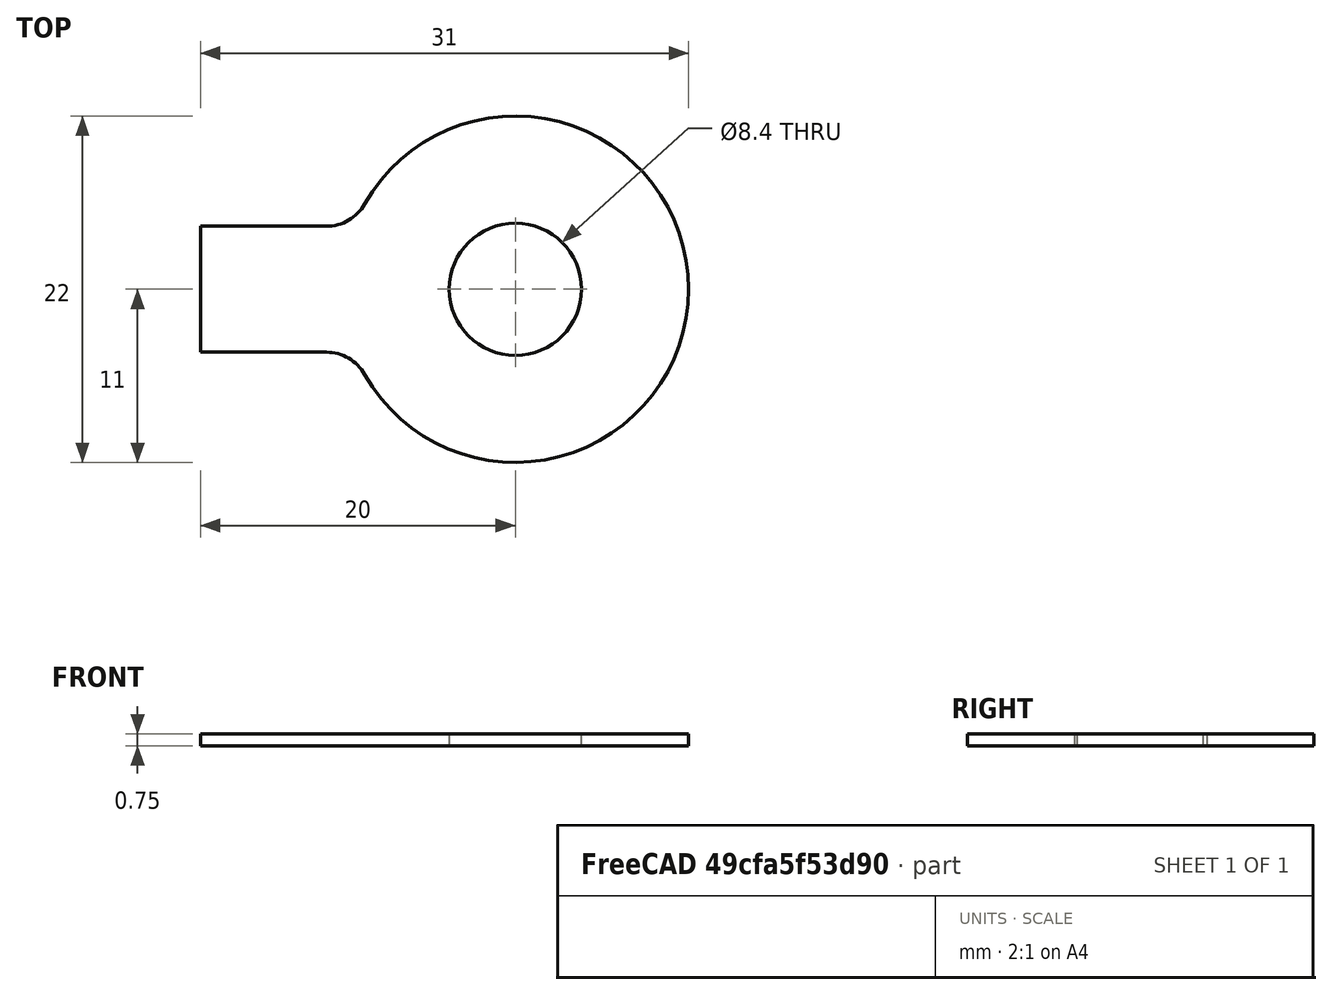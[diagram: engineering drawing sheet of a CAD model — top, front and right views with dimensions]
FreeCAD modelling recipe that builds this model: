
FCSTD DOCUMENT  (FreeCAD 0.15R4671 (Git))
Label: DIN93_M8TabWasher
License: CreativeCommons Attribution-ShareAlike
LicenseURL: http://creativecommons.org/licenses/by-sa/4.0/
objects: Sketcher::SketchObject×1, PartDesign::Pad×1
note: 3 computed .brp shape members not serialized (recipe doc carries the construction recipe); baked Part::Feature solids carry a one-line shape summary decoded from their .brp

FEATURE [Sketcher::SketchObject] Sketch
  sketch-geometry (7):
    g0: Circle CenterX=0 CenterY=0 CenterZ=0 NormalX=0 NormalY=0 NormalZ=1 Radius=4.2
    g1: LineSegment StartX=-20 StartY=4 StartZ=0 EndX=-12 EndY=4 EndZ=0
    g2: LineSegment StartX=-12 StartY=-4 StartZ=0 EndX=-20 EndY=-4 EndZ=0
    g3: LineSegment StartX=-20 StartY=-4 StartZ=0 EndX=-20 EndY=4 EndZ=0
    g4: ArcOfCircle CenterX=0 CenterY=0 CenterZ=0 NormalX=0 NormalY=0 NormalZ=1 Radius=11 StartAngle=3.65624 EndAngle=8.91013
    g5: ArcOfCircle CenterX=-12 CenterY=6.7857 CenterZ=0 NormalX=0 NormalY=0 NormalZ=1 Radius=2.7857 StartAngle=4.71239 EndAngle=5.76853
    g6: ArcOfCircle CenterX=-12 CenterY=-6.7857 CenterZ=0 NormalX=0 NormalY=0 NormalZ=1 Radius=2.7857 StartAngle=0.514656 EndAngle=1.5708
  constraints (22):
    c: Coincident(g0,g-1)
    c: Radius(g0) = 4.2
    c: Coincident(g2,g3)
    c: Coincident(g3,g1)
    c: Horizontal(g1)
    c: Horizontal(g2)
    c: Vertical(g3)
    c: Symmetric(g1,g2,g-1)
    c: Equal(g1,g3)
    c: Equal(g3,g2)
    c: DistanceY(g3) = 8
    c: DistanceX(g-1,g2) = -20
    c: Coincident(g4,g-1)
    c: Radius(g4) = 11
    c: Coincident(g5,g4)
    c: Coincident(g5,g1)
    c: Tangent(g5,g4)
    c: Coincident(g6,g2)
    c: Coincident(g6,g4)
    c: Tangent(g4,g6)
    c: Tangent(g6,g2)
    c: Tangent(g1,g5)
FEATURE [PartDesign::Pad] Pad
  Length = 0.75
  Length2 = 100
  Sketch = -> Sketch
  Type = 0
